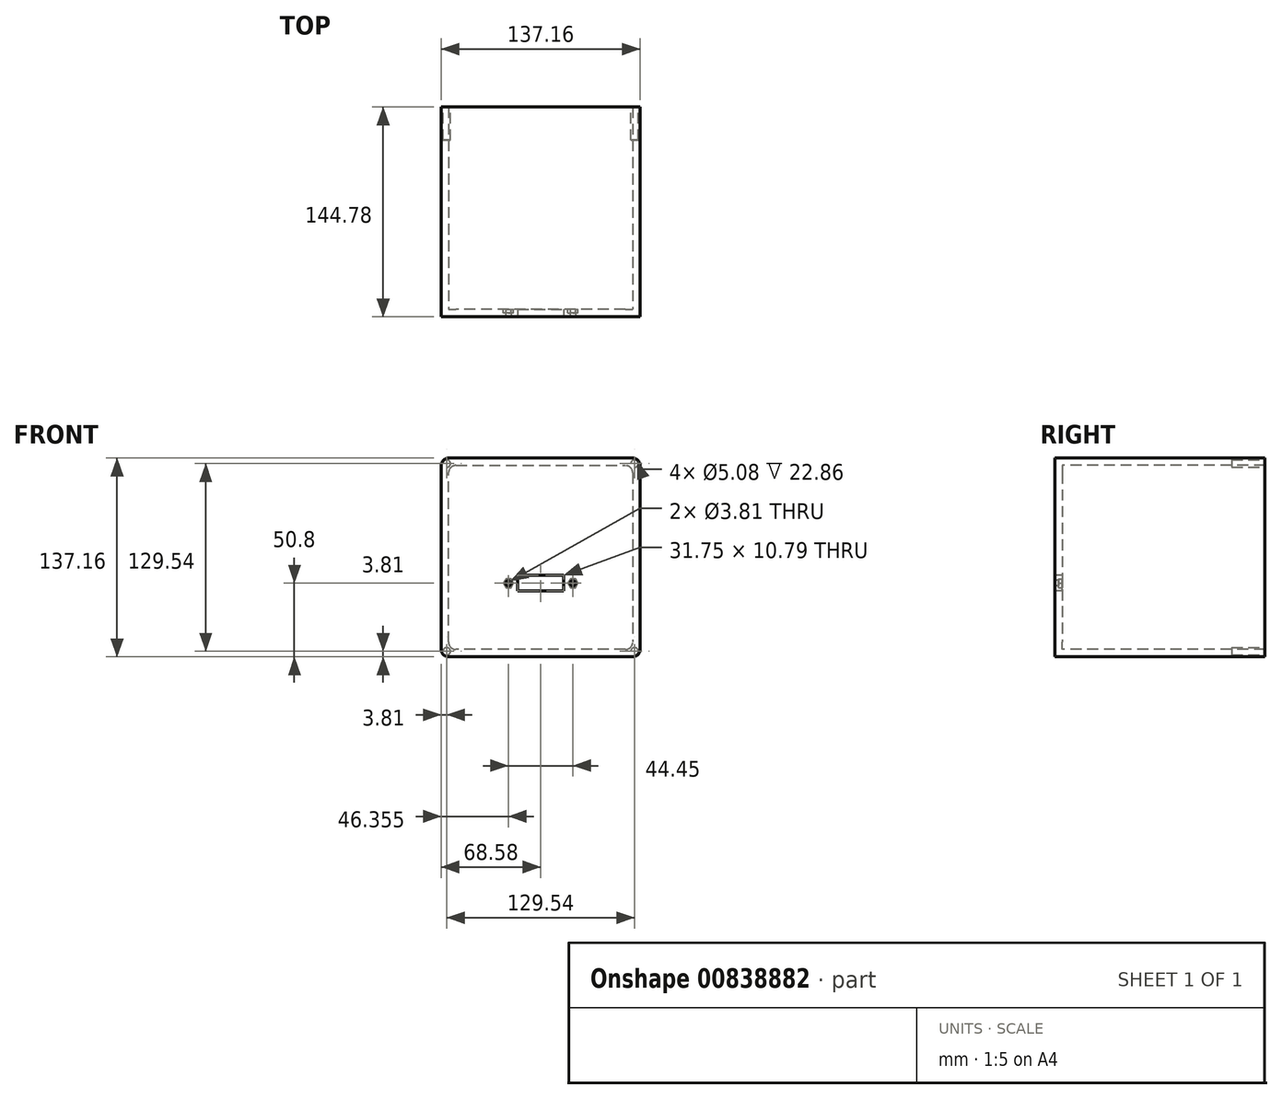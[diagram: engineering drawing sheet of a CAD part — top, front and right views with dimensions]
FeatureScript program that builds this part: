
annotation { "Feature Type Name" : "Feature", "Feature Type Description" : "" }
export const myFeature = defineFeature(function(context is Context, id is Id, definition is map)
    precondition{}
    {
        {
            var Q0;
            Q0=qCreatedBy(makeId("Front.planeOp"),FACE);
            var sketch = newSketch(context, id + "F0", { "sketchPlane" : qUnion([Q0])});
            skLineSegment(sketch, "E0.bottom", {"start": v(0, 0) * mm, "end": v(137.16, 0) * mm});
            skLineSegment(sketch, "E0.top", {"start": v(0, 137.16) * mm, "end": v(137.16, 137.16) * mm});
            skLineSegment(sketch, "E0.left", {"start": v(0, 0) * mm, "end": v(0, 137.16) * mm});
            skLineSegment(sketch, "E0.right", {"start": v(137.16, 0) * mm, "end": v(137.16, 137.16) * mm});
            skSolve(sketch);
        }
        {
            var Q0;
            Q0=makeQuery(id+"F0.imprint","IMPRINT",FACE,{"disambiguationData":[TD([[makeQuery(id+"F0.imprint","IMPRINT",EDGE,{"derivedFrom":sQuery(id+"F0.wireOp",EDGE,"E0.bottom")}),1.0]])]});
            extrude(context, id + "F1", {"entities" : qUnion([Q0]), "depth" : 5.08 * mm, "offsetDistance" : 25.4 * mm});
        }
        {
            var Q0;
            Q0=makeQuery(id+"F1.opExtrude","CAP_FACE",FACE,{"disambiguationData":[OSD([sQuery(id+"F0.wireOp",EDGE,"E0.bottom"),sQuery(id+"F0.wireOp",EDGE,"E0.top"),sQuery(id+"F0.wireOp",EDGE,"E0.left"),sQuery(id+"F0.wireOp",EDGE,"E0.right")])],"isStart":true});
            var sketch = newSketch(context, id + "F2", { "sketchPlane" : qUnion([Q0])});
            skLineSegment(sketch, "E1.bottom", {"start": v(-137.16, 137.16) * mm, "end": v(-132.08, 137.16) * mm});
            skLineSegment(sketch, "E1.top", {"start": v(-137.16, 0) * mm, "end": v(-132.08, 0) * mm});
            skLineSegment(sketch, "E1.left", {"start": v(-137.16, 137.16) * mm, "end": v(-137.16, 0) * mm});
            skLineSegment(sketch, "E1.right", {"start": v(-132.08, 137.16) * mm, "end": v(-132.08, 0) * mm});
            skLineSegment(sketch, "E2.bottom", {"start": v(0, 137.16) * mm, "end": v(-132.08, 137.16) * mm});
            skLineSegment(sketch, "E2.top", {"start": v(0, 132.08) * mm, "end": v(-132.08, 132.08) * mm});
            skLineSegment(sketch, "E2.left", {"start": v(0, 137.16) * mm, "end": v(0, 132.08) * mm});
            skLineSegment(sketch, "E2.right", {"start": v(-132.08, 137.16) * mm, "end": v(-132.08, 132.08) * mm});
            skLineSegment(sketch, "E3.bottom", {"start": v(-132.08, 5.08) * mm, "end": v(0, 5.08) * mm});
            skLineSegment(sketch, "E3.top", {"start": v(-132.08, 0) * mm, "end": v(0, 0) * mm});
            skLineSegment(sketch, "E3.left", {"start": v(-132.08, 5.08) * mm, "end": v(-132.08, 0) * mm});
            skLineSegment(sketch, "E3.right", {"start": v(0, 5.08) * mm, "end": v(0, 0) * mm});
            skLineSegment(sketch, "E4.bottom", {"start": v(-5.08, 5.08) * mm, "end": v(0, 5.08) * mm});
            skLineSegment(sketch, "E4.top", {"start": v(-5.08, 132.08) * mm, "end": v(0, 132.08) * mm});
            skLineSegment(sketch, "E4.left", {"start": v(-5.08, 5.08) * mm, "end": v(-5.08, 132.08) * mm});
            skLineSegment(sketch, "E4.right", {"start": v(0, 5.08) * mm, "end": v(0, 132.08) * mm});
            skSolve(sketch);
        }
        {
            var Q0;
            Q0 = qSketchRegion(id + "F2", true);
            extrude(context, id + "F3", {"entities" : qUnion([Q0]), "operationType" : NewBodyOperationType.ADD, "depth" : 139.7 * mm, "offsetDistance" : 25.4 * mm});
        }
        {
            var Q0;
            Q0=makeQuery(id+"F1.opExtrude","CAP_FACE",FACE,{"disambiguationData":[OSD([sQuery(id+"F0.wireOp",EDGE,"E0.bottom"),sQuery(id+"F0.wireOp",EDGE,"E0.top"),sQuery(id+"F0.wireOp",EDGE,"E0.left"),sQuery(id+"F0.wireOp",EDGE,"E0.right")])],"isStart":false});
            var sketch = newSketch(context, id + "F4", { "sketchPlane" : qUnion([Q0])});
            skLineSegment(sketch, "E5", {"start": v(68.58, 137.16) * mm, "end": v(68.58, 0) * mm});
            skLineSegment(sketch, "E6.bottom", {"start": v(84.46, 56.2) * mm, "end": v(52.7, 56.2) * mm});
            skLineSegment(sketch, "E6.top", {"start": v(84.46, 45.4) * mm, "end": v(52.7, 45.4) * mm});
            skLineSegment(sketch, "E6.left", {"start": v(84.46, 56.2) * mm, "end": v(84.46, 45.4) * mm});
            skLineSegment(sketch, "E6.right", {"start": v(52.7, 56.2) * mm, "end": v(52.7, 45.4) * mm});
            skPoint(sketch, "E6.middle", {"position": v(68.58, 50.8) * mm});
            skSolve(sketch);
        }
        {
            var Q0;
            Q0 = qSketchRegion(id + "F4", true);
            var Q1;
            Q1=makeQuery(id+"F1.opExtrude","CAP_FACE",FACE,{"disambiguationData":[OSD([sQuery(id+"F0.wireOp",EDGE,"E0.bottom"),sQuery(id+"F0.wireOp",EDGE,"E0.top"),sQuery(id+"F0.wireOp",EDGE,"E0.left"),sQuery(id+"F0.wireOp",EDGE,"E0.right")])],"isStart":true});
            extrude(context, id + "F5", {"entities" : qUnion([Q0]), "operationType" : NewBodyOperationType.REMOVE, "endBound" : BoundingType.UP_TO_SURFACE, "oppositeDirection" : true, "depth" : 25.4 * mm, "endBoundEntityFace" : qUnion([Q1]), "offsetDistance" : 25.4 * mm});
        }
        {
            var Q0;
            Q0=makeQuery(id+"F1.opExtrude","CAP_FACE",FACE,{"disambiguationData":[OSD([sQuery(id+"F0.wireOp",EDGE,"E0.bottom"),sQuery(id+"F0.wireOp",EDGE,"E0.top"),sQuery(id+"F0.wireOp",EDGE,"E0.left"),sQuery(id+"F0.wireOp",EDGE,"E0.right")])],"isStart":false});
            var sketch = newSketch(context, id + "F6", { "sketchPlane" : qUnion([Q0])});
            skCircle(sketch, "E7", {"center": v(90.8, 50.8) * mm, "radius": 1.9 * mm});
            skCircle(sketch, "E8", {"center": v(46.36, 50.8) * mm, "radius": 1.9 * mm});
            skLineSegment(sketch, "E9", {"start": v(46.36, 50.8) * mm, "end": v(90.8, 50.8) * mm});
            skLineSegment(sketch, "E10", {"start": v(52.7, 50.8) * mm, "end": v(84.46, 50.8) * mm});
            skPoint(sketch, "E11", {"position": v(68.58, 50.8) * mm});
            skSolve(sketch);
        }
        {
            var Q0;
            Q0 = qSketchRegion(id + "F6", true);
            var Q1;
            Q1=makeQuery(id+"F1.opExtrude","CAP_FACE",FACE,{"disambiguationData":[OSD([sQuery(id+"F0.wireOp",EDGE,"E0.bottom"),sQuery(id+"F0.wireOp",EDGE,"E0.top"),sQuery(id+"F0.wireOp",EDGE,"E0.left"),sQuery(id+"F0.wireOp",EDGE,"E0.right")])],"isStart":true});
            extrude(context, id + "F7", {"entities" : qUnion([Q0]), "operationType" : NewBodyOperationType.REMOVE, "endBound" : BoundingType.UP_TO_SURFACE, "oppositeDirection" : true, "depth" : 25.4 * mm, "endBoundEntityFace" : qUnion([Q1]), "offsetDistance" : 25.4 * mm});
        }
        {
            var Q0;
            Q0=makeQuery(id+"F3.boolean.opBoolean","MERGE",EDGE,{"derivedFrom":[makeQuery(id+"F1.opExtrude","SWEPT_EDGE",EDGE,{"disambiguationData":[OSD([sQuery(id+"F0.wireOp",EDGE,"E0.top"),sQuery(id+"F0.wireOp",EDGE,"E0.left")])]}),makeQuery(id+"F3.opExtrude","SWEPT_EDGE",EDGE,{"disambiguationData":[OSD([sQuery(id+"F2.wireOp",EDGE,"E2.bottom"),sQuery(id+"F2.wireOp",EDGE,"E2.left")])]})]});
            var Q1;
            Q1=makeQuery(id+"F3.boolean.opBoolean","MERGE",EDGE,{"derivedFrom":[makeQuery(id+"F1.opExtrude","SWEPT_EDGE",EDGE,{"disambiguationData":[OSD([sQuery(id+"F0.wireOp",EDGE,"E0.top"),sQuery(id+"F0.wireOp",EDGE,"E0.right")])]}),makeQuery(id+"F3.opExtrude","SWEPT_EDGE",EDGE,{"disambiguationData":[OSD([sQuery(id+"F2.wireOp",EDGE,"E1.bottom"),sQuery(id+"F2.wireOp",EDGE,"E1.left")])]})]});
            var Q2;
            Q2=makeQuery(id+"F3.boolean.opBoolean","MERGE",EDGE,{"derivedFrom":[makeQuery(id+"F1.opExtrude","SWEPT_EDGE",EDGE,{"disambiguationData":[OSD([sQuery(id+"F0.wireOp",EDGE,"E0.bottom"),sQuery(id+"F0.wireOp",EDGE,"E0.left")])]}),makeQuery(id+"F3.opExtrude","SWEPT_EDGE",EDGE,{"disambiguationData":[OSD([sQuery(id+"F2.wireOp",EDGE,"E3.top"),sQuery(id+"F2.wireOp",EDGE,"E3.right")])]})]});
            var Q3;
            Q3=makeQuery(id+"F3.boolean.opBoolean","MERGE",EDGE,{"derivedFrom":[makeQuery(id+"F1.opExtrude","SWEPT_EDGE",EDGE,{"disambiguationData":[OSD([sQuery(id+"F0.wireOp",EDGE,"E0.bottom"),sQuery(id+"F0.wireOp",EDGE,"E0.right")])]}),makeQuery(id+"F3.opExtrude","SWEPT_EDGE",EDGE,{"disambiguationData":[OSD([sQuery(id+"F2.wireOp",EDGE,"E1.top"),sQuery(id+"F2.wireOp",EDGE,"E1.left")])]})]});
            var Q4;
            Q4=makeQuery(id+"F3.opExtrude","SWEPT_EDGE",EDGE,{"disambiguationData":[OSD([sQuery(id+"F2.wireOp",EDGE,"E2.top"),sQuery(id+"F2.wireOp",EDGE,"E4.top"),sQuery(id+"F2.wireOp",EDGE,"E4.left")])]});
            var Q5;
            Q5=makeQuery(id+"F3.opExtrude","SWEPT_EDGE",EDGE,{"disambiguationData":[OSD([sQuery(id+"F2.wireOp",EDGE,"E1.right"),sQuery(id+"F2.wireOp",EDGE,"E2.top"),sQuery(id+"F2.wireOp",EDGE,"E2.right")])]});
            var Q6;
            Q6=makeQuery(id+"F3.opExtrude","SWEPT_EDGE",EDGE,{"disambiguationData":[OSD([sQuery(id+"F2.wireOp",EDGE,"E3.bottom"),sQuery(id+"F2.wireOp",EDGE,"E4.bottom"),sQuery(id+"F2.wireOp",EDGE,"E4.left")])]});
            var Q7;
            Q7=makeQuery(id+"F3.opExtrude","SWEPT_EDGE",EDGE,{"disambiguationData":[OSD([sQuery(id+"F2.wireOp",EDGE,"E1.right"),sQuery(id+"F2.wireOp",EDGE,"E3.bottom"),sQuery(id+"F2.wireOp",EDGE,"E3.left")])]});
            fillet(context, id + "F8", {"entities" : qUnion([Q0, Q1, Q2, Q3, Q4, Q5, Q6, Q7]), "radius" : 5.08 * mm, "tangentPropagation" : true, "allowEdgeOverflow" : false});
        }
        {
            var Q0;
            Q0=makeQuery(id+"F1.opExtrude","CAP_FACE",FACE,{"disambiguationData":[OSD([sQuery(id+"F0.wireOp",EDGE,"E0.bottom"),sQuery(id+"F0.wireOp",EDGE,"E0.top"),sQuery(id+"F0.wireOp",EDGE,"E0.left"),sQuery(id+"F0.wireOp",EDGE,"E0.right")])],"isStart":true});
            var sketch = newSketch(context, id + "F9", { "sketchPlane" : qUnion([Q0])});
            skCircle(sketch, "E12.cCircle", {"center": v(-90.8, 50.8) * mm, "radius": 3.04 * mm, "construction": true});
            skLineSegment(sketch, "E12.0", {"start": v(-92.56, 53.84) * mm, "end": v(-89.05, 53.84) * mm});
            skLineSegment(sketch, "E12.1", {"start": v(-89.05, 53.84) * mm, "end": v(-87.3, 50.8) * mm});
            skLineSegment(sketch, "E12.2", {"start": v(-87.3, 50.8) * mm, "end": v(-89.05, 47.76) * mm});
            skLineSegment(sketch, "E12.3", {"start": v(-89.05, 47.76) * mm, "end": v(-92.56, 47.76) * mm});
            skLineSegment(sketch, "E12.4", {"start": v(-92.56, 47.76) * mm, "end": v(-94.31, 50.8) * mm});
            skLineSegment(sketch, "E12.5", {"start": v(-94.31, 50.8) * mm, "end": v(-92.56, 53.84) * mm});
            skPoint(sketch, "E12.0.midPoint", {"position": v(-90.8, 53.84) * mm});
            skCircle(sketch, "E13.cCircle", {"center": v(-46.36, 50.8) * mm, "radius": 3.04 * mm, "construction": true});
            skLineSegment(sketch, "E13.0", {"start": v(-44.6, 53.84) * mm, "end": v(-42.85, 50.8) * mm});
            skLineSegment(sketch, "E13.1", {"start": v(-42.85, 50.8) * mm, "end": v(-44.6, 47.76) * mm});
            skLineSegment(sketch, "E13.2", {"start": v(-44.6, 47.76) * mm, "end": v(-48.1, 47.76) * mm});
            skLineSegment(sketch, "E13.3", {"start": v(-48.1, 47.76) * mm, "end": v(-49.86, 50.8) * mm});
            skLineSegment(sketch, "E13.4", {"start": v(-49.86, 50.8) * mm, "end": v(-48.1, 53.84) * mm});
            skLineSegment(sketch, "E13.5", {"start": v(-48.1, 53.84) * mm, "end": v(-44.6, 53.84) * mm});
            skPoint(sketch, "E13.0.midPoint", {"position": v(-43.73, 52.32) * mm});
            skSolve(sketch);
        }
        {
            var Q0;
            Q0 = qSketchRegion(id + "F9", true);
            extrude(context, id + "F10", {"entities" : qUnion([Q0]), "operationType" : NewBodyOperationType.REMOVE, "oppositeDirection" : true, "depth" : 2.54 * mm, "offsetDistance" : 25.4 * mm});
        }
        {
            var Q0;
            Q0=makeQuery(id+"F3.opExtrude","CAP_FACE",FACE,{"disambiguationData":[OSD([sQuery(id+"F2.wireOp",EDGE,"E1.bottom"),sQuery(id+"F2.wireOp",EDGE,"E1.top"),sQuery(id+"F2.wireOp",EDGE,"E1.left"),sQuery(id+"F2.wireOp",EDGE,"E1.right"),sQuery(id+"F2.wireOp",EDGE,"E2.bottom"),sQuery(id+"F2.wireOp",EDGE,"E2.top"),sQuery(id+"F2.wireOp",EDGE,"E2.left"),sQuery(id+"F2.wireOp",EDGE,"E3.bottom"),sQuery(id+"F2.wireOp",EDGE,"E3.top"),sQuery(id+"F2.wireOp",EDGE,"E3.right"),sQuery(id+"F2.wireOp",EDGE,"E4.left"),sQuery(id+"F2.wireOp",EDGE,"E4.right")])],"isStart":false});
            var sketch = newSketch(context, id + "F11", { "sketchPlane" : qUnion([Q0])});
            skLineSegment(sketch, "E14.bottom", {"start": v(-133.35, 133.35) * mm, "end": v(-3.81, 133.35) * mm});
            skLineSegment(sketch, "E14.top", {"start": v(-133.35, 3.81) * mm, "end": v(-3.81, 3.81) * mm});
            skLineSegment(sketch, "E14.left", {"start": v(-133.35, 133.35) * mm, "end": v(-133.35, 3.81) * mm});
            skLineSegment(sketch, "E14.right", {"start": v(-3.81, 133.35) * mm, "end": v(-3.81, 3.81) * mm});
            skLineSegment(sketch, "E15", {"start": v(-133.35, 68.58) * mm, "end": v(-3.81, 68.58) * mm});
            skPoint(sketch, "E16", {"position": v(-68.58, 68.58) * mm});
            skLineSegment(sketch, "E17", {"start": v(-68.58, 137.16) * mm, "end": v(-68.58, 0) * mm});
            skCircle(sketch, "E18", {"center": v(-3.81, 133.35) * mm, "radius": 2.54 * mm});
            skCircle(sketch, "E19", {"center": v(-3.81, 3.81) * mm, "radius": 2.54 * mm});
            skCircle(sketch, "E20", {"center": v(-133.35, 3.81) * mm, "radius": 2.54 * mm});
            skCircle(sketch, "E21", {"center": v(-133.35, 133.35) * mm, "radius": 2.54 * mm});
            skSolve(sketch);
        }
        {
            var Q0;
            {var subQ0=sQuery(id+"F11.wireOp",EDGE,"E14.left");var subQ1=sQuery(id+"F11.wireOp",EDGE,"E14.bottom");var subQ2=makeQuery(id+"F11.imprint","INTERSECT",VERTEX,{"derivedFrom":[subQ1,subQ0]});Q0=makeQuery(id+"F11.imprint","IMPRINT",FACE,{"disambiguationData":[TD([[makeQuery(id+"F11.imprint","IMPRINT",EDGE,{"disambiguationData":[TD([[subQ2,-1.0]])],"derivedFrom":subQ1}),1.0]])]});}
            var Q1;
            {var subQ0=sQuery(id+"F11.wireOp",EDGE,"E14.left");var subQ1=sQuery(id+"F11.wireOp",EDGE,"E14.bottom");var subQ2=makeQuery(id+"F11.imprint","INTERSECT",VERTEX,{"derivedFrom":[subQ1,subQ0]});Q1=makeQuery(id+"F11.imprint","IMPRINT",FACE,{"disambiguationData":[TD([[makeQuery(id+"F11.imprint","IMPRINT",EDGE,{"disambiguationData":[TD([[subQ2,-1.0]])],"derivedFrom":subQ1}),-1.0]])]});}
            var Q2;
            {var subQ0=sQuery(id+"F11.wireOp",EDGE,"E14.left");var subQ1=sQuery(id+"F11.wireOp",EDGE,"E14.top");var subQ2=makeQuery(id+"F11.imprint","INTERSECT",VERTEX,{"derivedFrom":[subQ1,subQ0]});Q2=makeQuery(id+"F11.imprint","IMPRINT",FACE,{"disambiguationData":[TD([[makeQuery(id+"F11.imprint","IMPRINT",EDGE,{"disambiguationData":[TD([[subQ2,-1.0]])],"derivedFrom":subQ1}),1.0]])]});}
            var Q3;
            {var subQ0=sQuery(id+"F11.wireOp",EDGE,"E14.left");var subQ1=sQuery(id+"F11.wireOp",EDGE,"E14.top");var subQ2=makeQuery(id+"F11.imprint","INTERSECT",VERTEX,{"derivedFrom":[subQ1,subQ0]});Q3=makeQuery(id+"F11.imprint","IMPRINT",FACE,{"disambiguationData":[TD([[makeQuery(id+"F11.imprint","IMPRINT",EDGE,{"disambiguationData":[TD([[subQ2,-1.0]])],"derivedFrom":subQ1}),-1.0]])]});}
            var Q4;
            {var subQ0=sQuery(id+"F11.wireOp",EDGE,"E14.right");var subQ1=sQuery(id+"F11.wireOp",EDGE,"E14.top");var subQ2=makeQuery(id+"F11.imprint","INTERSECT",VERTEX,{"derivedFrom":[subQ1,subQ0]});Q4=makeQuery(id+"F11.imprint","IMPRINT",FACE,{"disambiguationData":[TD([[makeQuery(id+"F11.imprint","IMPRINT",EDGE,{"disambiguationData":[TD([[subQ2,1.0]])],"derivedFrom":subQ1}),1.0]])]});}
            var Q5;
            {var subQ0=sQuery(id+"F11.wireOp",EDGE,"E14.right");var subQ1=sQuery(id+"F11.wireOp",EDGE,"E14.top");var subQ2=makeQuery(id+"F11.imprint","INTERSECT",VERTEX,{"derivedFrom":[subQ1,subQ0]});Q5=makeQuery(id+"F11.imprint","IMPRINT",FACE,{"disambiguationData":[TD([[makeQuery(id+"F11.imprint","IMPRINT",EDGE,{"disambiguationData":[TD([[subQ2,1.0]])],"derivedFrom":subQ1}),-1.0]])]});}
            var Q6;
            {var subQ0=sQuery(id+"F11.wireOp",EDGE,"E14.right");var subQ1=sQuery(id+"F11.wireOp",EDGE,"E14.bottom");var subQ2=makeQuery(id+"F11.imprint","INTERSECT",VERTEX,{"derivedFrom":[subQ1,subQ0]});Q6=makeQuery(id+"F11.imprint","IMPRINT",FACE,{"disambiguationData":[TD([[makeQuery(id+"F11.imprint","IMPRINT",EDGE,{"disambiguationData":[TD([[subQ2,1.0]])],"derivedFrom":subQ1}),-1.0]])]});}
            var Q7;
            {var subQ0=sQuery(id+"F11.wireOp",EDGE,"E14.right");var subQ1=sQuery(id+"F11.wireOp",EDGE,"E14.bottom");var subQ2=makeQuery(id+"F11.imprint","INTERSECT",VERTEX,{"derivedFrom":[subQ1,subQ0]});Q7=makeQuery(id+"F11.imprint","IMPRINT",FACE,{"disambiguationData":[TD([[makeQuery(id+"F11.imprint","IMPRINT",EDGE,{"disambiguationData":[TD([[subQ2,1.0]])],"derivedFrom":subQ1}),1.0]])]});}
            var Q8;
            Q8=sQuery(id+"F11.wireOp",EDGE,"E21");
            var Q9;
            Q9=sQuery(id+"F11.wireOp",EDGE,"E18");
            var Q10;
            Q10=sQuery(id+"F11.wireOp",EDGE,"E19");
            var Q11;
            Q11=sQuery(id+"F11.wireOp",EDGE,"E20");
            extrude(context, id + "F12", {"entities" : qUnion([Q0, Q1, Q2, Q3, Q4, Q5, Q6, Q7]), "operationType" : NewBodyOperationType.REMOVE, "surfaceEntities" : qUnion([Q8, Q9, Q10, Q11]), "oppositeDirection" : true, "depth" : 22.86 * mm, "offsetDistance" : 25.4 * mm});
        }
    });
